# Revit family: DC_Holyoake_MEQ_EC-125_12
name_source: partatom
category: Air Terminals
revit_build: Autodesk Revit MEP 2013 (Build: 20120221_2030(x64)
units: mm (PartAtom-declared; Revit-internal decimal feet)

## types (2) — shared parameters
Actual Face Size Height = 831 mm  [stored 2.72638 ft]
Actual Face Size Width = 831 mm  [stored 2.72638 ft]
Actual Neck Size Height = 783 mm  [stored 2.5689 ft]
Actual Neck Size Width = 783 mm  [stored 2.5689 ft]
Description = Eggcrate Return/ Exhuast Air Grilles shall be Holyoake Model EC125 of aluminium construction. The Eggcrate Core shall be 12.5mm x 12.5mm x 12.5mm and fitted in an extruded aluminium Flanged Frame. Eggcrate  Grilles shall be finished in powdercoat and fitted with accessories and dampers where indicated as manufactured by Holyoake.
Face Size Height = 831 mm  [stored 2.72638 ft]
Face Size Width = 831 mm  [stored 2.72638 ft]
Holyoake Product Range = Holyoake Return Air Grille
Manufacturer = Holyoake
Material Body = Holyoake White
Material Face = Holyoake White
Max Flow = 4700.0 L/s
Min Flow = 20.0 L/s
Noise Level NC Max = 60 NC
Noise Level NC Min = < 10 NC
Nom Neck Height = 800 mm  [stored 2.62467 ft]
Nom Neck Width = 800 mm  [stored 2.62467 ft]
Type Comments = Egg Crate Return Air Grille
URL = http://www.holyoake.com

## per-type parameters (varying)
| type | Grille Depth | Static Pressure Max | Static Pressure Min |
| EC-125 | 22 mm  [stored 0.0721785 ft] | 80.0 Pa | 3.0 Pa |
| EC-125/OBD | 72 mm  [stored 0.23622 ft] | 0.0 Pa | 0.0 Pa |

note: column(s) folded — value = type name in every type: Model

note: [stored X ft] marks values corroborated as IEEE doubles in the binary element streams (Revit-internal decimal feet)

## geometry (parser evidence)
native form markers: Blend x12, Sweep x1
no freeform markers — native parametric forms only
